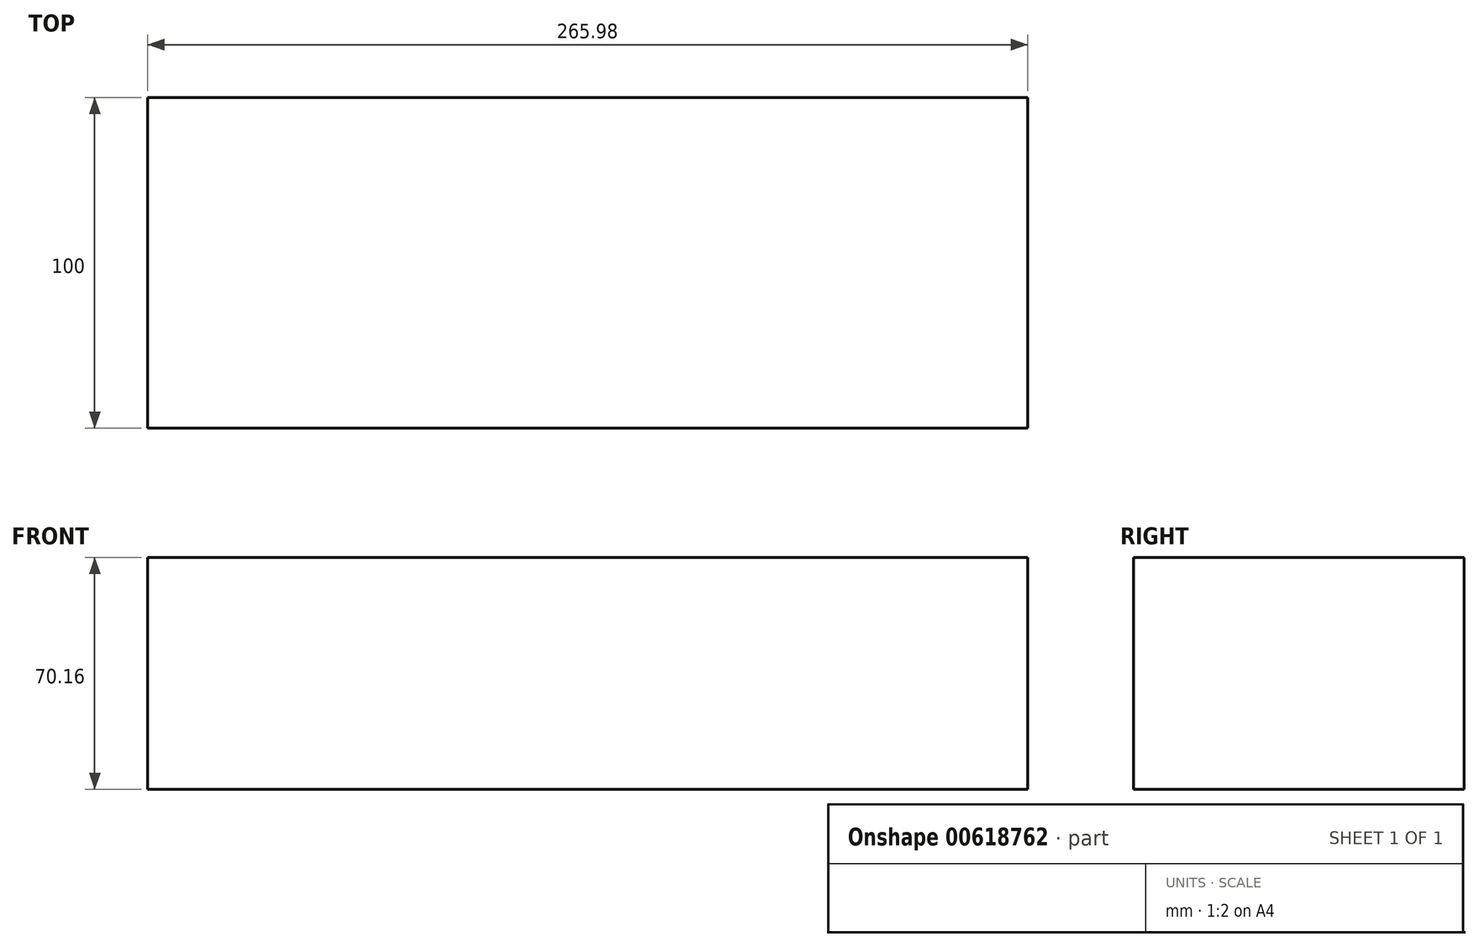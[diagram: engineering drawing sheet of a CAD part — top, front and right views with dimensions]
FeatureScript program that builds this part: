
annotation { "Feature Type Name" : "Feature", "Feature Type Description" : "" }
export const myFeature = defineFeature(function(context is Context, id is Id, definition is map)
    precondition{}
    {
        {
            var Q0;
            Q0=qCreatedBy(makeId("Front.planeOp"),FACE);
            var sketch = newSketch(context, id + "F0", { "sketchPlane" : qUnion([Q0])});
            skLineSegment(sketch, "E0.bottom", {"start": v(133, 35.08) * mm, "end": v(-133, 35.08) * mm});
            skLineSegment(sketch, "E0.top", {"start": v(133, -35.08) * mm, "end": v(-133, -35.08) * mm});
            skLineSegment(sketch, "E0.left", {"start": v(133, 35.08) * mm, "end": v(133, -35.08) * mm});
            skLineSegment(sketch, "E0.right", {"start": v(-133, 35.08) * mm, "end": v(-133, -35.08) * mm});
            skPoint(sketch, "E0.middle", {"position": v(0, 0) * mm});
            skSolve(sketch);
        }
        {
            var Q0;
            Q0=makeQuery(id+"F0.imprint","IMPRINT",FACE,{"disambiguationData":[TD([[makeQuery(id+"F0.imprint","IMPRINT",EDGE,{"derivedFrom":sQuery(id+"F0.wireOp",EDGE,"E0.bottom")}),1.0]])]});
            extrude(context, id + "F1", {"entities" : qUnion([Q0]), "depth" : 100 * mm, "offsetDistance" : 25 * mm});
        }
    });
